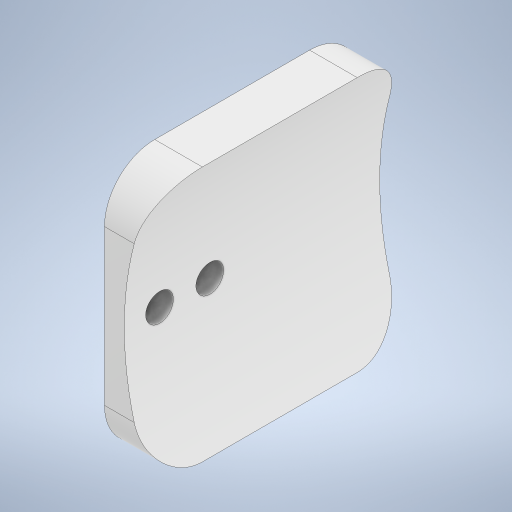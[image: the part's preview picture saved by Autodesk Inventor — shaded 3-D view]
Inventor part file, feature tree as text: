
AUTODESK INVENTOR PART (.ipt)
format: ipt  version: 2023 (Build 270158030, 158C)  size: 243,200 bytes
history: native  units: in
note: dims shown in document units (in); Inventor stores cm internally (conversion verified against a paired STEP export)
features: extrude x2, sketch x2, fillet x1
ambient origin geometry x8: Origin, YZ Plane, XZ Plane, XY Plane, X Axis, Y Axis, Z Axis, Center Point
bodies: Solid1 (feature_tree)
feature tree (5):
  extrude  "Extrusion1"  Depth=2.5591in
  extrude  "Extrusion2"  Depth=0.3937in TaperAngle=0.0deg
  fillet  "Fillet1"  [1 undecoded]
  sketch  "Sketch1"  dims[d0=4.808in d1=2.5591in]
  sketch  "Sketch2"  dims[d2=2.0in d3=2.0in d4=0.0in d6=0.0in d7=0.0in d8=0.2165in d9=0.2756in d10=0.3937in d11=0.3937in]
note: 1 required parameter value undecoded (feature->parameter linkage not recoverable at this tier; creation-order binding heuristic only, values carry confidence <= 0.55)
